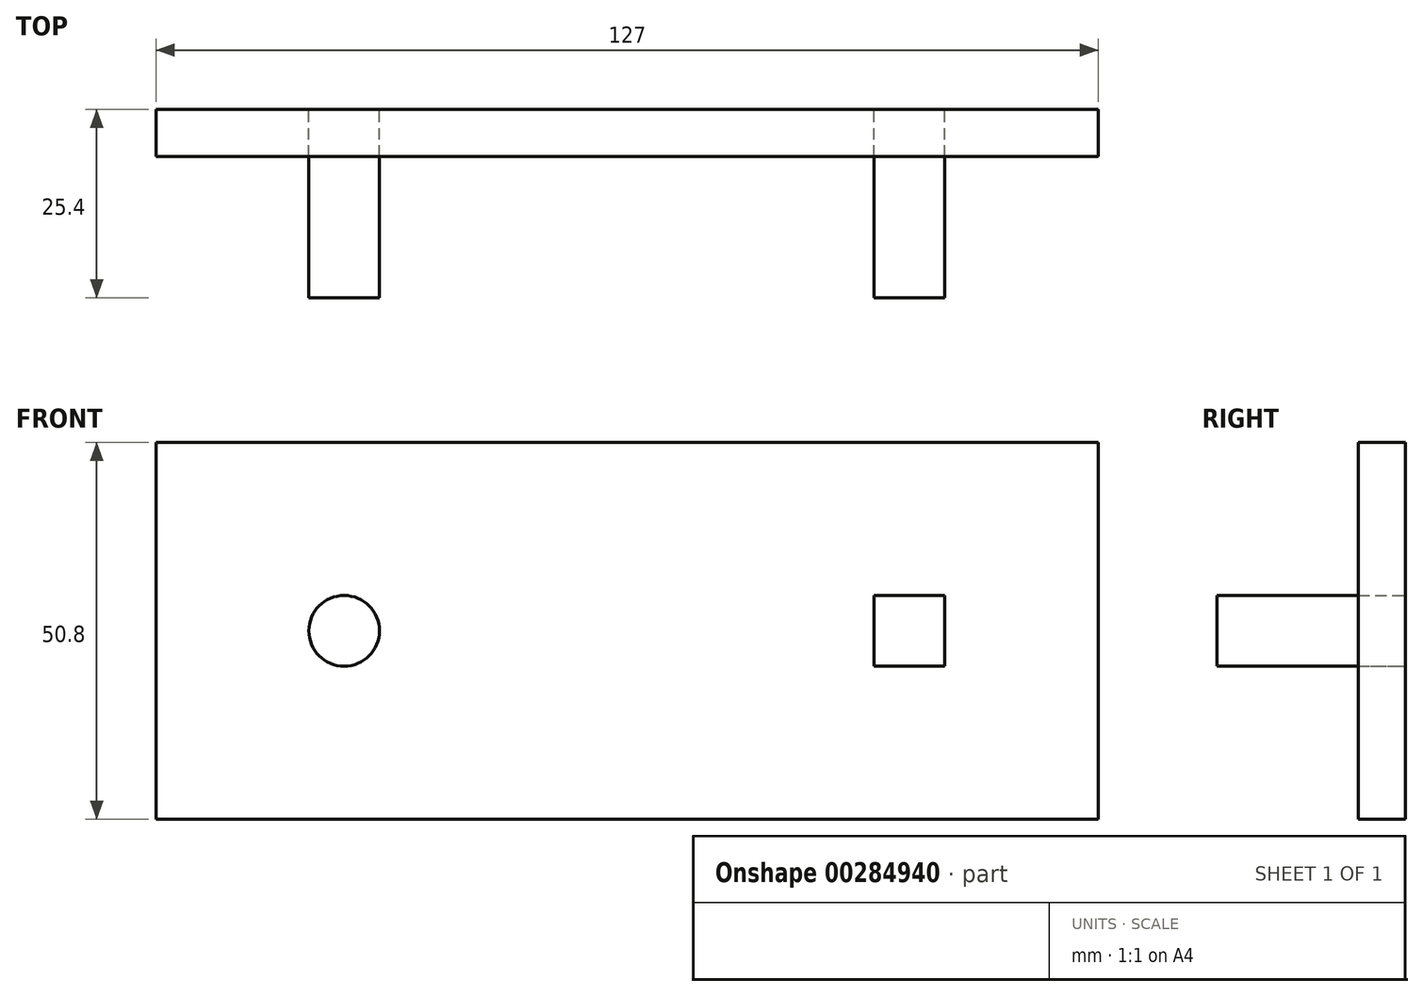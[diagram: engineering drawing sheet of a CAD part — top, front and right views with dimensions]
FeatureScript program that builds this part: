
annotation { "Feature Type Name" : "Feature", "Feature Type Description" : "" }
export const myFeature = defineFeature(function(context is Context, id is Id, definition is map)
    precondition{}
    {
        {
            var Q0;
            Q0=qCreatedBy(makeId("Front.planeOp"),FACE);
            var sketch = newSketch(context, id + "F0", { "sketchPlane" : qUnion([Q0])});
            skLineSegment(sketch, "E0.bottom", {"start": v(63.5, 25.4) * mm, "end": v(-63.5, 25.4) * mm});
            skLineSegment(sketch, "E0.top", {"start": v(63.5, -25.4) * mm, "end": v(-63.5, -25.4) * mm});
            skLineSegment(sketch, "E0.left", {"start": v(63.5, 25.4) * mm, "end": v(63.5, -25.4) * mm});
            skLineSegment(sketch, "E0.right", {"start": v(-63.5, 25.4) * mm, "end": v(-63.5, -25.4) * mm});
            skPoint(sketch, "E0.middle", {"position": v(0, 0) * mm});
            skSolve(sketch);
        }
        {
            var Q0;
            Q0=qCreatedBy(makeId("Front.planeOp"),FACE);
            var sketch = newSketch(context, id + "F1", { "sketchPlane" : qUnion([Q0])});
            skCircle(sketch, "E1", {"center": v(-38.15, 0) * mm, "radius": 4.76 * mm});
            skLineSegment(sketch, "E2.bottom", {"start": v(42.81, 4.76) * mm, "end": v(33.29, 4.76) * mm});
            skLineSegment(sketch, "E2.top", {"start": v(42.81, -4.76) * mm, "end": v(33.29, -4.76) * mm});
            skLineSegment(sketch, "E2.left", {"start": v(42.81, 4.76) * mm, "end": v(42.81, -4.76) * mm});
            skLineSegment(sketch, "E2.right", {"start": v(33.29, 4.76) * mm, "end": v(33.29, -4.76) * mm});
            skPoint(sketch, "E2.middle", {"position": v(38.05, 0) * mm});
            skSolve(sketch);
        }
        {
            var Q0;
            {var subQ0=sQuery(id+"F1.wireOp",EDGE,"5Zl7hWcx-Vfif-6HsS-f2ZM-u7ULnNQ5xVKX");var subQ1=sQuery(id+"F1.wireOp",EDGE,"ShflypP2-Z43F-BW97-jndV-6qC142foT7Cp");var subQ2=makeQuery(id+"F1.imprint","INTERSECT",VERTEX,{"derivedFrom":[subQ1,subQ0]});Q0=makeQuery(id+"F1.imprint","IMPRINT",FACE,{"disambiguationData":[TD([[makeQuery(id+"F1.imprint","IMPRINT",EDGE,{"disambiguationData":[TD([[subQ2,1.0]])],"derivedFrom":subQ1}),-1.0]])]});}
            var Q1;
            {var subQ0=sQuery(id+"F1.wireOp",EDGE,"5Zl7hWcx-Vfif-6HsS-f2ZM-u7ULnNQ5xVKX");var subQ1=sQuery(id+"F1.wireOp",EDGE,"ShflypP2-Z43F-BW97-jndV-6qC142foT7Cp");var subQ2=makeQuery(id+"F1.imprint","INTERSECT",VERTEX,{"derivedFrom":[subQ1,subQ0]});Q1=makeQuery(id+"F1.imprint","IMPRINT",FACE,{"disambiguationData":[TD([[makeQuery(id+"F1.imprint","IMPRINT",EDGE,{"disambiguationData":[TD([[subQ2,1.0]])],"derivedFrom":subQ1}),1.0]])]});}
            var Q2;
            {var subQ1=sQuery(id+"F1.wireOp",EDGE,"E2.bottom");Q2=makeQuery(id+"F1.imprint","IMPRINT",FACE,{"disambiguationData":[TD([[makeQuery(id+"F1.imprint","IMPRINT",EDGE,{"derivedFrom":subQ1}),1.0]])]});}
            var Q3;
            Q3=makeQuery(id+"F0.imprint","IMPRINT",FACE,{"disambiguationData":[TD([[makeQuery(id+"F0.imprint","IMPRINT",EDGE,{"derivedFrom":sQuery(id+"F0.wireOp",EDGE,"E0.bottom")}),1.0]])]});
            extrude(context, id + "F2", {"entities" : qUnion([Q0, Q1, Q2, Q3]), "depth" : 6.35 * mm});
        }
        {
            var Q0;
            Q0 = qSketchRegion(id + "F1", true);
            extrude(context, id + "F3", {"entities" : qUnion([Q0]), "depth" : 25.4 * mm});
        }
    });
